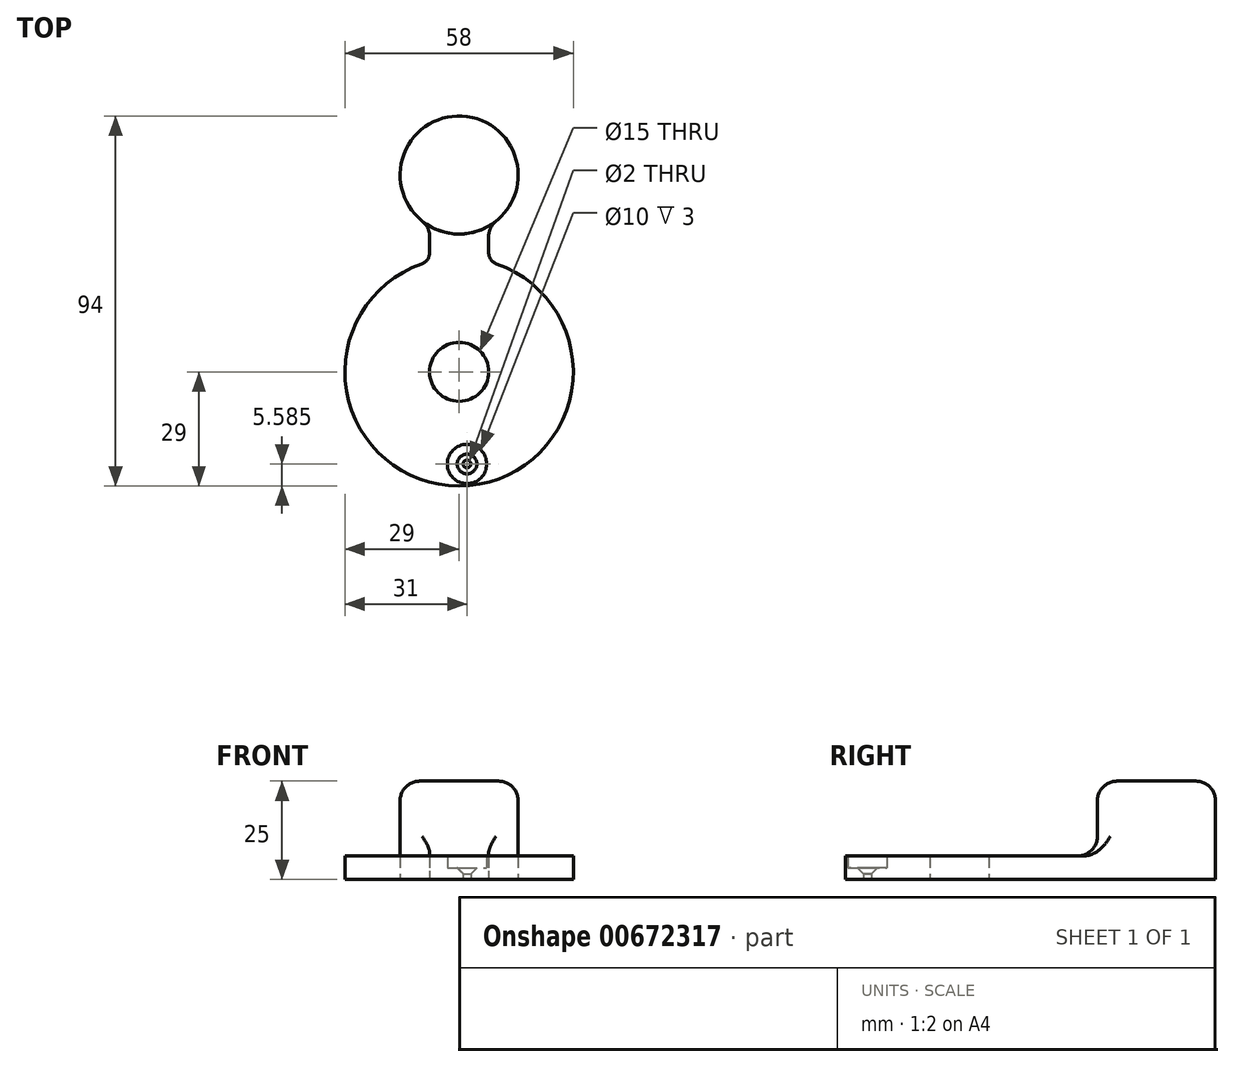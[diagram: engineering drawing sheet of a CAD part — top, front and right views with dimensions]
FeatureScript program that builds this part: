
annotation { "Feature Type Name" : "Feature", "Feature Type Description" : "" }
export const myFeature = defineFeature(function(context is Context, id is Id, definition is map)
    precondition{}
    {
        {
            var Q0;
            Q0=qCreatedBy(makeId("Top.planeOp"),FACE);
            var sketch = newSketch(context, id + "F0", { "sketchPlane" : qUnion([Q0])});
            skCircle(sketch, "E0", {"center": v(0, 0) * mm, "radius": 29 * mm});
            skCircle(sketch, "E1", {"center": v(0, 0) * mm, "radius": 7.5 * mm});
            skLineSegment(sketch, "E2", {"start": v(-7.5, 28.01) * mm, "end": v(-7.5, 58.01) * mm});
            skLineSegment(sketch, "E3", {"start": v(-7.5, 58.01) * mm, "end": v(7.5, 58.01) * mm});
            skLineSegment(sketch, "E4", {"start": v(7.5, 58.01) * mm, "end": v(7.5, 28.01) * mm});
            skLineSegment(sketch, "E5", {"start": v(0, 75.5) * mm, "end": v(0, -67.29) * mm, "construction": true});
            skCircle(sketch, "E6", {"center": v(2, -23.41) * mm, "radius": 1 * mm});
            skSolve(sketch);
        }
        {
            var Q0;
            Q0=makeQuery(id+"F0.imprint","IMPRINT",FACE,{"disambiguationData":[TD([[makeQuery(id+"F0.imprint","IMPRINT",EDGE,{"derivedFrom":sQuery(id+"F0.wireOp",EDGE,"E1")}),-1.0]])]});
            var Q1;
            {var subQ0=sQuery(id+"F0.wireOp",EDGE,"E2");Q1=makeQuery(id+"F0.imprint","IMPRINT",FACE,{"disambiguationData":[TD([[makeQuery(id+"F0.imprint","IMPRINT",EDGE,{"derivedFrom":subQ0}),-1.0]])]});}
            extrude(context, id + "F1", {"entities" : qUnion([Q0, Q1]), "depth" : 6 * mm, "offsetDistance" : 25 * mm});
        }
        {
            var Q0;
            Q0=qCreatedBy(makeId("Right.planeOp"),FACE);
            cPlane(context, id + "F2", {"entities" : qUnion([Q0]), "cplaneType" : CPlaneType.OFFSET, "offset" : 2 * mm, "width" : 150 * mm, "height" : 150 * mm});
        }
        {
            var Q0;
            Q0=qCreatedBy(id+"F2.planeOp",FACE);
            var sketch = newSketch(context, id + "F3", { "sketchPlane" : qUnion([Q0])});
            skLineSegment(sketch, "E7.0", {"start": v(-24.41, 6) * mm, "end": v(-22.41, 6) * mm, "construction": true});
            skLineSegment(sketch, "E8", {"start": v(-23.41, 6) * mm, "end": v(-23.41, 0) * mm});
            skLineSegment(sketch, "E9", {"start": v(-23.41, 0) * mm, "end": v(-24.41, 0) * mm});
            skLineSegment(sketch, "E10", {"start": v(-24.41, 0) * mm, "end": v(-24.41, 1.5) * mm});
            skLineSegment(sketch, "E11", {"start": v(-24.41, 1.5) * mm, "end": v(-25.91, 3) * mm});
            skLineSegment(sketch, "E12", {"start": v(-25.91, 3) * mm, "end": v(-28.41, 3) * mm});
            skLineSegment(sketch, "E13", {"start": v(-28.41, 3) * mm, "end": v(-28.41, 6) * mm});
            skLineSegment(sketch, "E14", {"start": v(-28.41, 6) * mm, "end": v(-23.41, 6) * mm});
            skSolve(sketch);
        }
        {
            var Q0;
            Q0 = qSketchRegion(id + "F3", true);
            var Q1;
            Q1=sQuery(id+"F3.wireOp",EDGE,"E8");
            revolve(context, id + "F4", {"operationType" : NewBodyOperationType.REMOVE, "entities" : qUnion([Q0]), "axis" : qUnion([Q1]), "revolveType" : RevolveType.FULL, "oppositeDirection" : true});
        }
        {
            var Q0;
            Q0=makeQuery(id+"F1.opExtrude","SWEPT_EDGE",EDGE,{"disambiguationData":[OSD([sQuery(id+"F0.wireOp",EDGE,"E0"),sQuery(id+"F0.wireOp",EDGE,"E4")])]});
            var Q1;
            Q1=makeQuery(id+"F1.opExtrude","SWEPT_EDGE",EDGE,{"disambiguationData":[OSD([sQuery(id+"F0.wireOp",EDGE,"E0"),sQuery(id+"F0.wireOp",EDGE,"E2")])]});
            fillet(context, id + "F5", {"entities" : qUnion([Q0, Q1]), "radius" : 3 * mm, "tangentPropagation" : true, "allowEdgeOverflow" : false});
        }
        {
            var Q0;
            Q0=qCreatedBy(makeId("Top.planeOp"),FACE);
            var sketch = newSketch(context, id + "F6", { "sketchPlane" : qUnion([Q0])});
            skCircle(sketch, "E15", {"center": v(0, 50) * mm, "radius": 15 * mm});
            skSolve(sketch);
        }
        {
            var Q0;
            Q0 = qSketchRegion(id + "F6", true);
            extrude(context, id + "F7", {"entities" : qUnion([Q0]), "operationType" : NewBodyOperationType.ADD, "depth" : 25 * mm, "offsetDistance" : 25 * mm});
        }
        {
            var Q0;
            Q0=makeQuery(id+"F7.boolean.opBoolean","INTERSECT",EDGE,{"derivedFrom":[makeQuery(id+"F1.opExtrude","SWEPT_FACE",FACE,{"disambiguationData":[OSD([sQuery(id+"F0.wireOp",EDGE,"E4")])]}),makeQuery(id+"F7.opExtrude","SWEPT_FACE",FACE,{"disambiguationData":[OSD([sQuery(id+"F6.wireOp",EDGE,"E15")])]})]});
            var Q1;
            Q1=makeQuery(id+"F7.boolean.opBoolean","INTERSECT",EDGE,{"derivedFrom":[makeQuery(id+"F1.opExtrude","SWEPT_FACE",FACE,{"disambiguationData":[OSD([sQuery(id+"F0.wireOp",EDGE,"E2")])]}),makeQuery(id+"F7.opExtrude","SWEPT_FACE",FACE,{"disambiguationData":[OSD([sQuery(id+"F6.wireOp",EDGE,"E15")])]})]});
            fillet(context, id + "F8", {"entities" : qUnion([Q0, Q1]), "radius" : 5 * mm, "tangentPropagation" : true, "allowEdgeOverflow" : false});
        }
        {
            var Q0;
            Q0=makeQuery(id+"F7.boolean.opBoolean","INTERSECT",EDGE,{"derivedFrom":[makeQuery(id+"F1.opExtrude","CAP_FACE",FACE,{"disambiguationData":[OSD([sQuery(id+"F0.wireOp",EDGE,"E0"),sQuery(id+"F0.wireOp",EDGE,"E1"),sQuery(id+"F0.wireOp",EDGE,"E2"),sQuery(id+"F0.wireOp",EDGE,"E3"),sQuery(id+"F0.wireOp",EDGE,"E4"),sQuery(id+"F0.wireOp",EDGE,"E6")])],"isStart":false}),makeQuery(id+"F7.opExtrude","SWEPT_FACE",FACE,{"disambiguationData":[OSD([sQuery(id+"F6.wireOp",EDGE,"E15")])]})]});
            fillet(context, id + "F9", {"entities" : qUnion([Q0]), "radius" : 5 * mm, "tangentPropagation" : true, "allowEdgeOverflow" : false});
        }
        {
            var Q0;
            Q0=makeQuery(id+"F7.opExtrude","CAP_EDGE",EDGE,{"disambiguationData":[OSD([sQuery(id+"F6.wireOp",EDGE,"E15")])],"isStart":false});
            fillet(context, id + "F10", {"entities" : qUnion([Q0]), "radius" : 5 * mm, "tangentPropagation" : true, "allowEdgeOverflow" : false});
        }
    });
